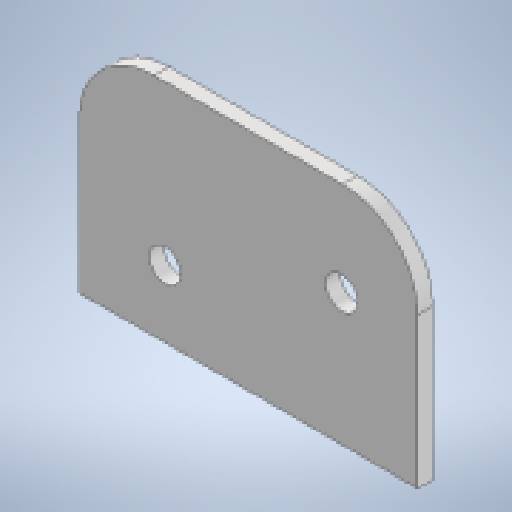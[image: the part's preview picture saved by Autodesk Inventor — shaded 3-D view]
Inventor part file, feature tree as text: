
AUTODESK INVENTOR PART (.ipt)
format: ipt  version: 2025 (Build 290162010, 162A)  size: 154,624 bytes
history: native  units: mm
features: sketch x2, sheet_metal_op x1, hole x1, fillet x1, other x1
ambient origin geometry x8: Origin, YZ Plane, XZ Plane, XY Plane, X Axis, Y Axis, Z Axis, Center Point
bodies: Solid1 (feature_tree)
feature tree (6):
  sheet_metal_op  "Face1"
  hole  "Hole1"  [1 undecoded]
  fillet  "Fillet1"  Radius=8.0mm
  sketch  "Sketch1"  dims[d0=180.0mm d1=120.0mm d2=8.0mm]
  other  "Plate1"
  sketch  "Sketch2"  dims[d3=17.0mm d4=6.0mm d5=4.0mm d6=2.0mm d7=90.0deg d8=8.0mm d9=20.594885mm d16=2.0mm d17=100.0mm d18=25.0mm d19=25.0mm d20=12.217305mm]
note: 1 required parameter value undecoded (feature->parameter linkage not recoverable at this tier; creation-order binding heuristic only, values carry confidence <= 0.55)
